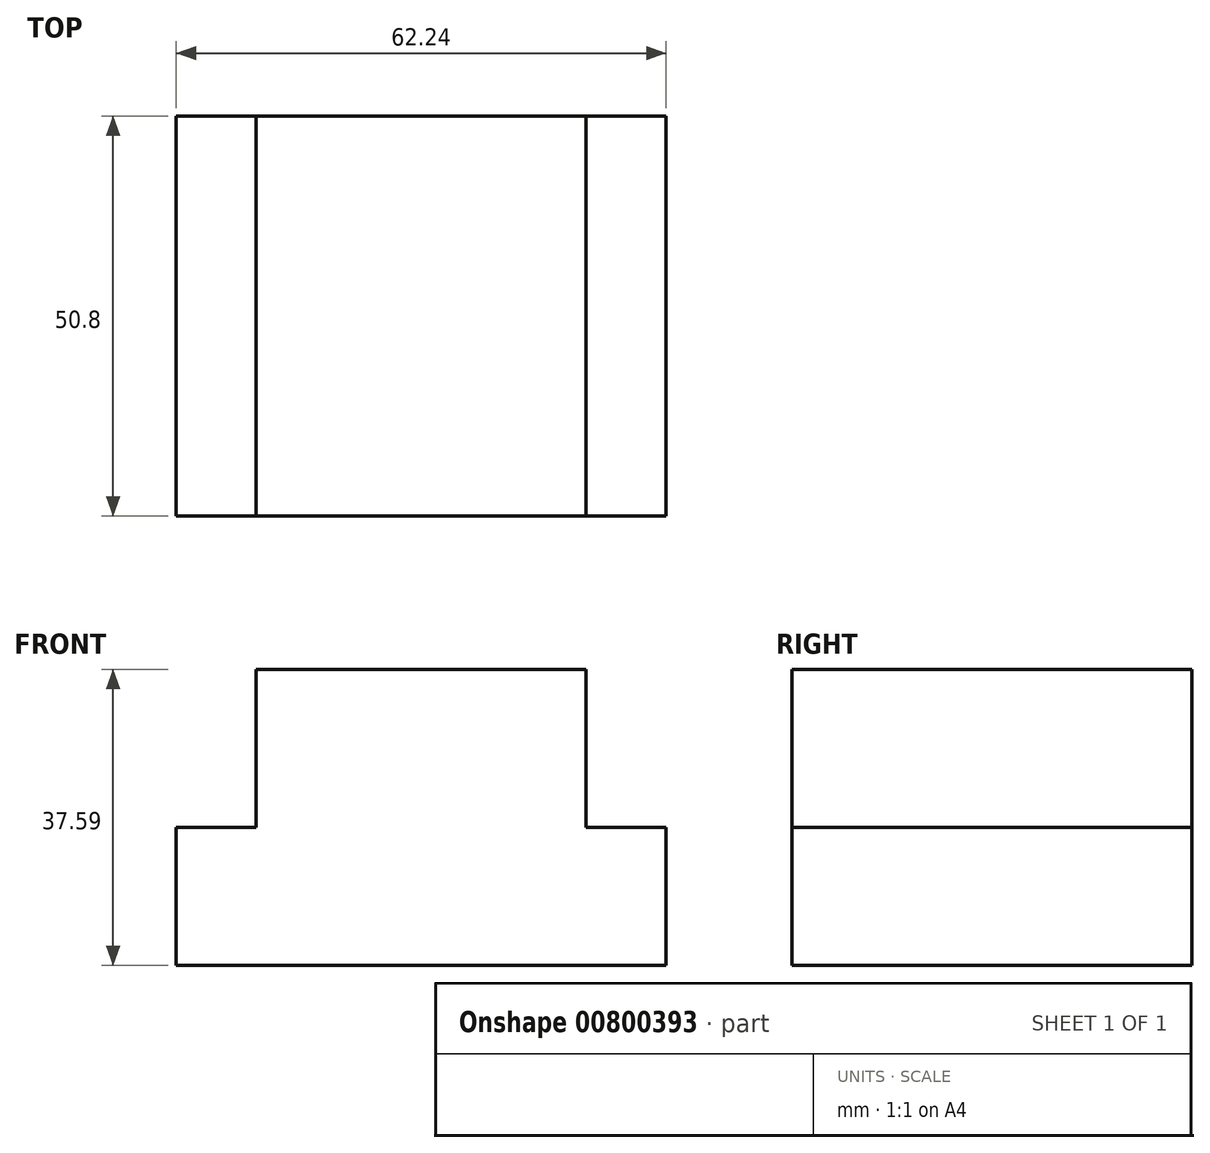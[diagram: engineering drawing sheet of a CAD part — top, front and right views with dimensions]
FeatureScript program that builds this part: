
annotation { "Feature Type Name" : "Feature", "Feature Type Description" : "" }
export const myFeature = defineFeature(function(context is Context, id is Id, definition is map)
    precondition{}
    {
        {
            var Q0;
            Q0=qCreatedBy(makeId("Front.planeOp"),FACE);
            var sketch = newSketch(context, id + "F0", { "sketchPlane" : qUnion([Q0])});
            skLineSegment(sketch, "E0.bottom", {"start": v(-31.12, -10.29) * mm, "end": v(31.12, -10.29) * mm});
            skLineSegment(sketch, "E0.top", {"start": v(-31.12, -27.81) * mm, "end": v(31.12, -27.81) * mm});
            skLineSegment(sketch, "E0.left", {"start": v(-31.12, -10.29) * mm, "end": v(-31.12, -27.81) * mm});
            skLineSegment(sketch, "E0.right", {"start": v(31.12, -10.29) * mm, "end": v(31.12, -27.81) * mm});
            skLineSegment(sketch, "E1.bottom", {"start": v(-20.96, -10.29) * mm, "end": v(20.96, -10.29) * mm});
            skLineSegment(sketch, "E1.top", {"start": v(-20.96, 9.78) * mm, "end": v(20.96, 9.78) * mm});
            skLineSegment(sketch, "E1.left", {"start": v(-20.96, -10.29) * mm, "end": v(-20.96, 9.78) * mm});
            skLineSegment(sketch, "E1.right", {"start": v(20.96, -10.29) * mm, "end": v(20.96, 9.78) * mm});
            skLineSegment(sketch, "E2", {"start": v(0, 0) * mm, "end": v(0, 45.6) * mm, "construction": true});
            skSolve(sketch);
        }
        {
            var Q0;
            Q0 = qSketchRegion(id + "F0", true);
            extrude(context, id + "F1", {"entities" : qUnion([Q0]), "depth" : 25.4 * mm, "offsetDistance" : 25.4 * mm, "hasSecondDirection" : true, "secondDirectionOppositeDirection" : true, "secondDirectionDepth" : 25.4 * mm});
        }
    });
